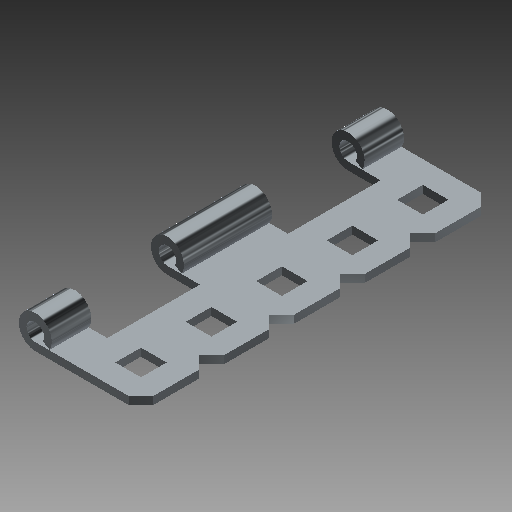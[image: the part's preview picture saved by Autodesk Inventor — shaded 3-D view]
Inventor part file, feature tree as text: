
AUTODESK INVENTOR PART (.ipt)
format: ipt  version: 2018 (Build 220112000, 112)  size: 200,704 bytes
history: native  units: in
note: dims shown in document units (in); Inventor stores cm internally (conversion verified against a paired STEP export)
features: extrude x7, other x5, sketch x3, pattern_linear x1
ambient origin geometry x8: Origin, YZ Plane, XZ Plane, XY Plane, X Axis, Y Axis, Z Axis, Center Point
bodies: Solid1 (feature_tree)
feature tree (16):
  extrude  "Extrusion1"  Depth=2.5in TaperAngle=0.0deg
  extrude  "Extrusion2"  Depth=0.5in
  pattern_linear  "Rectangular Pattern1"  Spacing1=0.0in  [1 undecoded]
  sketch  "Sketch1"  dims[d0=2.5in d1=0.0in d2=0.25in d3=0.0in]
  sketch  "Sketch2"  dims[d4=0.25in d5=0.0in d6=1.9685in d8=0.5in]
  sketch  "Sketch3"  dims[d9=0.0in d10=0.0in d11=0.0in d12=0.0in d13=0.0in d14=0.0in d15=0.0in d16=0.0in d17=0.0in d18=0.0in]
  other  "Srf1"
  other  "Srf2"
  other  "Srf3"
  other  "Srf4"
  other  "Srf5"
  extrude  "ExtrusionSrf1"  TaperAngle=0.0deg  [1 undecoded]
  extrude  "ExtrusionSrf2"  TaperAngle=0.0deg  [1 undecoded]
  extrude  "ExtrusionSrf3"  TaperAngle=0.0deg  [1 undecoded]
  extrude  "ExtrusionSrf4"  TaperAngle=0.0deg  [1 undecoded]
  extrude  "ExtrusionSrf5"  TaperAngle=0.0deg  [1 undecoded]
note: 6 required parameter values undecoded (feature->parameter linkage not recoverable at this tier; creation-order binding heuristic only, values carry confidence <= 0.55)
